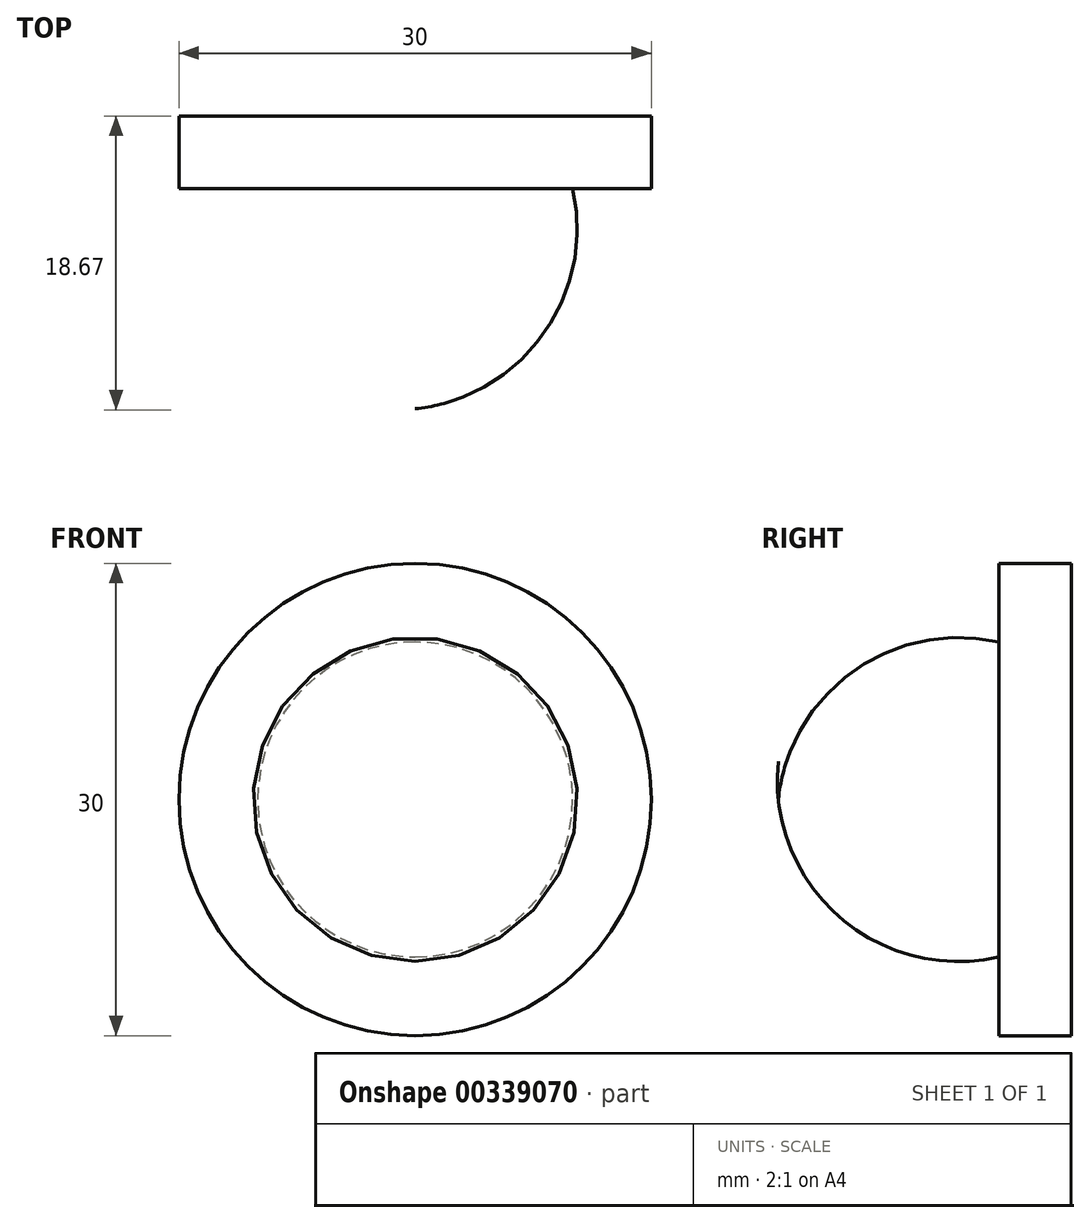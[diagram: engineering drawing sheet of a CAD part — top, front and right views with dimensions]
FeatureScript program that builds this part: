
annotation { "Feature Type Name" : "Feature", "Feature Type Description" : "" }
export const myFeature = defineFeature(function(context is Context, id is Id, definition is map)
    precondition{}
    {
        {
            var Q0;
            Q0=qCreatedBy(makeId("Top.planeOp"),FACE);
            var sketch = newSketch(context, id + "F0", { "sketchPlane" : qUnion([Q0])});
            skLineSegment(sketch, "E0", {"start": v(-22.5, 11.12) * mm, "end": v(-7.5, 11.12) * mm});
            skLineSegment(sketch, "E1", {"start": v(-7.5, 11.12) * mm, "end": v(-7.5, -7.48) * mm});
            skLineSegment(sketch, "E2", {"start": v(-22.5, 11.12) * mm, "end": v(-22.5, 6.52) * mm});
            skLineSegment(sketch, "E3", {"start": v(-22.5, 6.52) * mm, "end": v(-17.5, 6.52) * mm});
            skArc(sketch, "E4", {"start": v(-17.5, 6.52) * mm, "mid": v(-15.65, -2.73) * mm, "end": v(-7.5, -7.48) * mm});
            skSolve(sketch);
        }
        {
            var Q0;
            Q0=makeQuery(id+"F0.imprint","IMPRINT",FACE,{"disambiguationData":[TD([[makeQuery(id+"F0.imprint","IMPRINT",EDGE,{"derivedFrom":sQuery(id+"F0.wireOp",EDGE,"E0")}),-1.0]])]});
            var Q1;
            Q1=sQuery(id+"F0.wireOp",EDGE,"E1");
            revolve(context, id + "F1", {"surfaceOperationType" : NewSurfaceOperationType.NEW, "entities" : qUnion([Q0]), "axis" : qUnion([Q1]), "revolveType" : RevolveType.FULL});
        }
    });
